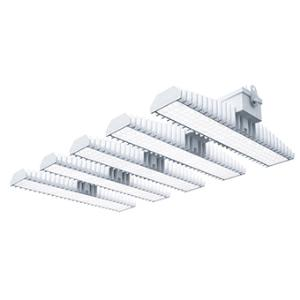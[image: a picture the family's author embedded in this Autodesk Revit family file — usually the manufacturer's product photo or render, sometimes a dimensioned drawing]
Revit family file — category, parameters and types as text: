
# Revit family: 3f_filippi_-_3f_lem_medio_3f_filippi_-_58897_a0812_-_3f_lem_5_led_250_cr_medio___vs_d2cb
name_source: partatom
category: Lighting Fixtures
units: mm (PartAtom-declared; Revit-internal decimal feet)

## family parameters
Cut with Voids When Loaded = No
Host = Face
Light Source = No
Part Type = Normal
Room Calculation Point = No
Round Connector Dimension = Use Diameter
Shared = No

## types (1)
- 3F Filippi - 3F LEM Medio (1 x LED, 33664 lm, 274 W, 4000 K)
    Apparent Load = 274 VA
    Approval mark = CE
    CIE Flux Codes = 77 92 98 100 100
    Color Rendering = 80
    Color Temperature = 4000 K
    Control Gear = Electronic ballast
    Default Elevation = 1800 mm
    Description = Industrial luminaire with high light output and high luminous efficiency designed with the most innovative technologies for environments with temperature up to 55°C.

ILLUMINOTECHNICAL
Luminous efficiency 100% (DLOR 98%, ULOR 2%).
Initial luminous flux of the luminaire 33664 lm.
Medium distribution with rectangular shape.
Installation Interdistance Transv.D = 0.87 x hu - Long.D = 0.87 x hu.
Tabular UGR (CIE 117 - 4H-8H; S=0.25H; 70/50/20): RUG 21.2 - 21.2.
Beam angle: 58° - 57°.
Luminous efficacy 123 lm/W.
Lifetime (L93/B10): 30000 h. (tq+25°C)
Lifetime (L90/B10): 50000 h. (tq+25°C)
Lifetime (L85/B10): 80000 h. (tq+25°C)
Lifetime (L80/B10): 100000 h. (tq+25°C)
Lifetime (L85/B10): 50000 h. (tq+55°C)
Sudden decreased luminous flux after 50000 hours: 0% (C0).
Photobiological safety in compliance with IEC/TR 62778: RG0 risk exempt, (IEC 62471).
In compliance with IEC/EN 62722-2-1 - IEC/EN 62717 standards.

SOURCE
5 Mid-Power linear LED modules 50W/840.
Energy efficiency class (UE 2019/2020 - UE 2019/2015): C.
CIE 13.3 Colour rendering index: CRI >80 (R9 <50%).
IES TM-30 Fidelity Index: Rf = 84 Rg = 95.
CCT nominal colour temperature 4000 K.
Colour initial tolerance (MacAdam): SDCM 3.

MECHANICAL
Passive modular heatsinks in die-casted aluminium, painted in white colour.
To optimize the thermal management of the LED module, the heatsinks are oversized and provided with self-cleaning of cooling fins.
Wiring body in aluminium and galvanised steel anchored solidly to the sinks and thermally separated.
3F Lens lenses with high luminous efficiency, transparent methacrylate (PMMA), fixed to the LED modules.
Fixing brackets in stainless steel.
Luminaire with limited surface temperature. - D - (EN 60598-2-24)
Dimensions: 952x542 mm, height 133 mm. Weight 24.07 kg.
IP65 protection degree.
Mechanical strength to impacts IK06 (1 joule).
Glow-wire test resistance 650°C.

ELECTRICAL
Halogen Free electronic wiring 230V-50/60Hz, power factor 0.97, THD <25%, constant output current, class I, 3 driver.
Power of the luminaire 274 W.
ENEC - CE.
SAFE FLICKER: PstLM=<1 and SVM=<0.4 (IEC TR 61547-1 and IEC TR 63158), to ensure a more comfortable and safe light.
Luminaire compliant with EN 60598-2-22 for power supply from a centralised emergency system CPSS (Central Power Supply System), not incorporated in the luminaire - high risk areas excluded. The default power and flux are 100% in AC and 100% in DC.
Ambient temperature from -30°C to +55°C.
Temperature class T6 max 85°C.
Quick connection via M20 3P connector with 9-13 mm tightening range.
Power unit positioned on a separate compartment by the LED module to ensure optimum temperatures of cabling components, to be inspectable and maintainable.
Relative humidity UR: <85%.

INSTALLATION
Ceiling / Suspended / Wall.
All accessories dedicated to this product are available on the Catalog and on our website www.3F-Filippi.com.

ACCESSORIES
A0812 - Anti-glare microprismatic VS moulded glass, tempered, not flammable, with sealing gasket.
One required for each light module. The pack contains 10 pieces.

APPLICATIONS
In commercial environments, exhibition and industrial areas, stores, open areas.
Applications with high ambient temperature up to 55°C.
Environments in which it is necessary a total protection against falling fragments (eg environments with foodstuffs or machines with moving parts or with extreme temperature changes), use luminaires with polycarbonate lenses.

WARNING
Fixture not suitable for cold stores with an ambient temperature <0°C and/or relative humidity >85%.
Luminaire designed for disposal/recycling at end-of-life.
Replaceable (LED only) light source by a professional. Replaceable control gear by a professional.
    Height = 133 mm  [stored 0.436352 ft]
    Lamp = 1 x LED
    Lamp Light Flux = 33664 lm
    Lamp Power = 274 W
    Lamp count = 1
    Length = 952 mm
    Lifetime = 50000 h
    Luminous efficacy = 123 lm/W
    Manufacturer = 3F Filippi
    ModVariant = No
    Model = 3F Filippi - 58897+A0812 - 3F LEM 5 LED 250 CR MEDIO + VS
    Mounting Place = Ceiling
    Mounting Type = Pendant
    Number of Poles = 1
    OnlyDefault = Yes
    Power Factor = 1
    Product Name = 3F Filippi - 3F LEM Medio
    Product group = pendant luminaire
    ProductGroupID = 9
    Protection Class = Protection class I
    Protection Degree = IP 65
    RLX_Detail_Level = 1
    RLX_Emergency_Light_Flux = 0 lm
    RLX_Emergency_Type = 0
    RLX_Emergency_Type_DB = No
    RlxData = <blob elided: 129921 chars, md5=271bad5c>
    Socket = socket
    Standby Power = 0 W
    System Light Flux = 33664 lm
    System Power = 274 W
    Type Comments = Product without accessories
    Type Image = 3f_filippi_-_lem_5__a0812.jpg
    URL = http://relux.com
    VarID = ---
    Voltage = 0 V
    Weight = 0.00 kg
    Width = 542 mm

note: [stored X ft] marks values corroborated as IEEE doubles in the binary element streams (Revit-internal decimal feet)

## geometry (parser evidence)
native form markers: Blend x4, Sweep x10
no freeform markers — native parametric forms only
